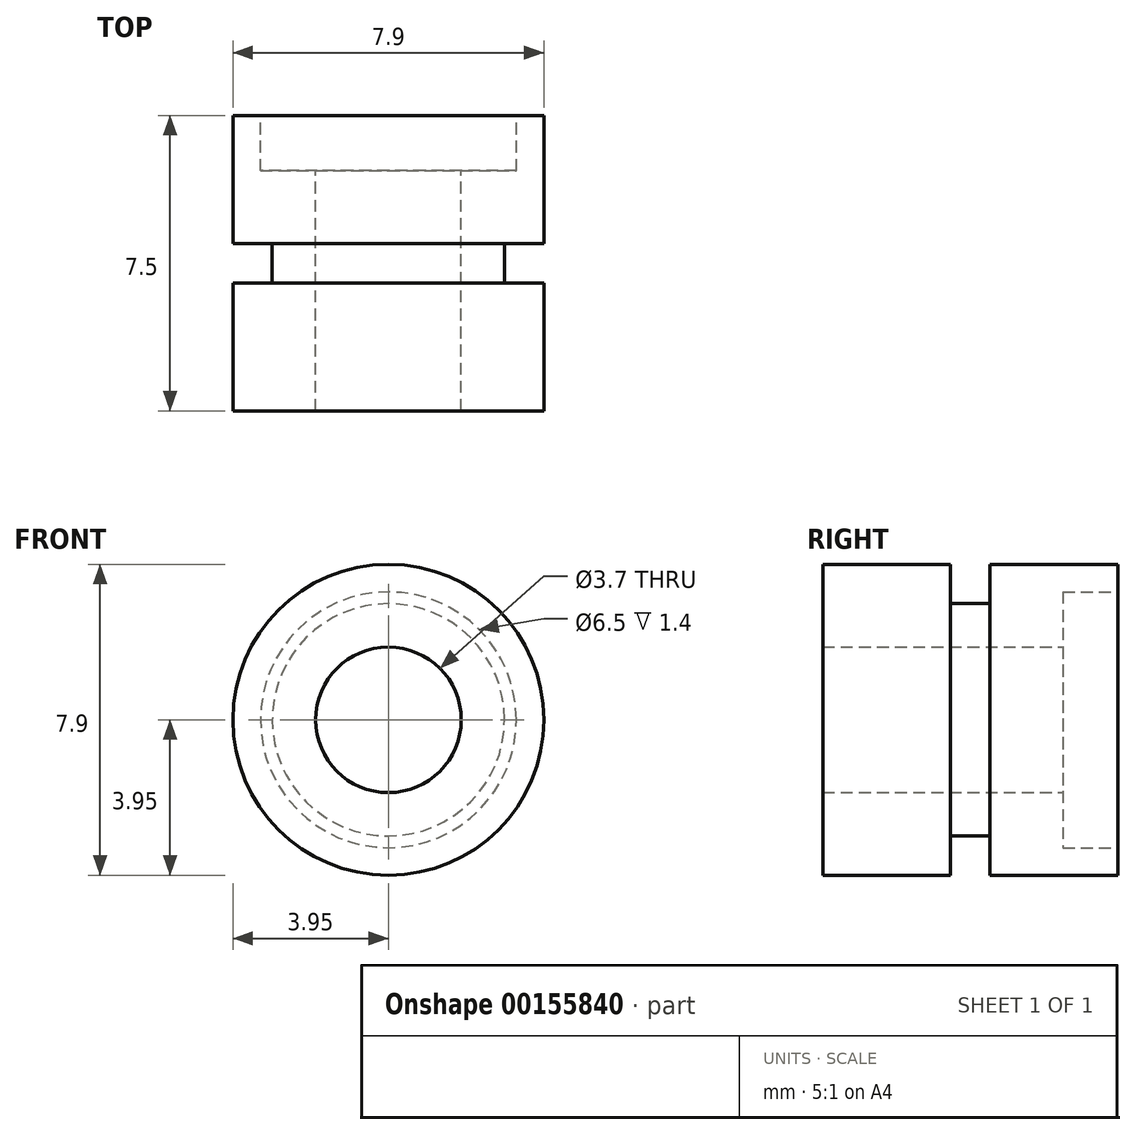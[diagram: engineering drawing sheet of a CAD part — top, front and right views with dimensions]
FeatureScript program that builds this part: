
annotation { "Feature Type Name" : "Feature", "Feature Type Description" : "" }
export const myFeature = defineFeature(function(context is Context, id is Id, definition is map)
    precondition{}
    {
        {
            var Q0;
            Q0=qCreatedBy(makeId("Right.planeOp"),FACE);
            var sketch = newSketch(context, id + "F0", { "sketchPlane" : qUnion([Q0])});
            skLineSegment(sketch, "E0", {"start": v(11.47, 0) * mm, "end": v(0, 0) * mm, "construction": true});
            skLineSegment(sketch, "E1", {"start": v(6.1, 1.85) * mm, "end": v(0, 1.85) * mm});
            skLineSegment(sketch, "E2", {"start": v(6.1, 1.85) * mm, "end": v(6.1, 3.25) * mm});
            skLineSegment(sketch, "E3", {"start": v(7.5, 3.25) * mm, "end": v(6.1, 3.25) * mm});
            skLineSegment(sketch, "E4", {"start": v(7.5, 3.25) * mm, "end": v(7.5, 3.95) * mm});
            skLineSegment(sketch, "E5", {"start": v(4.25, 3.95) * mm, "end": v(7.5, 3.95) * mm});
            skLineSegment(sketch, "E6", {"start": v(4.25, 3.95) * mm, "end": v(4.25, 2.95) * mm});
            skLineSegment(sketch, "E7", {"start": v(3.25, 2.95) * mm, "end": v(4.25, 2.95) * mm});
            skLineSegment(sketch, "E8", {"start": v(3.25, 2.95) * mm, "end": v(3.25, 3.95) * mm});
            skLineSegment(sketch, "E9", {"start": v(0, 3.95) * mm, "end": v(3.25, 3.95) * mm});
            skLineSegment(sketch, "E10", {"start": v(0, 3.95) * mm, "end": v(0, 1.85) * mm});
            skSolve(sketch);
        }
        {
            var Q0;
            Q0=makeQuery(id+"F0.imprint","IMPRINT",FACE,{"disambiguationData":[TD([[makeQuery(id+"F0.imprint","IMPRINT",EDGE,{"derivedFrom":sQuery(id+"F0.wireOp",EDGE,"E1")}),-1.0]])]});
            var Q1;
            Q1=sQuery(id+"F0.wireOp",EDGE,"E0");
            revolve(context, id + "F1", {"entities" : qUnion([Q0]), "axis" : qUnion([Q1]), "revolveType" : RevolveType.FULL});
        }
    });
